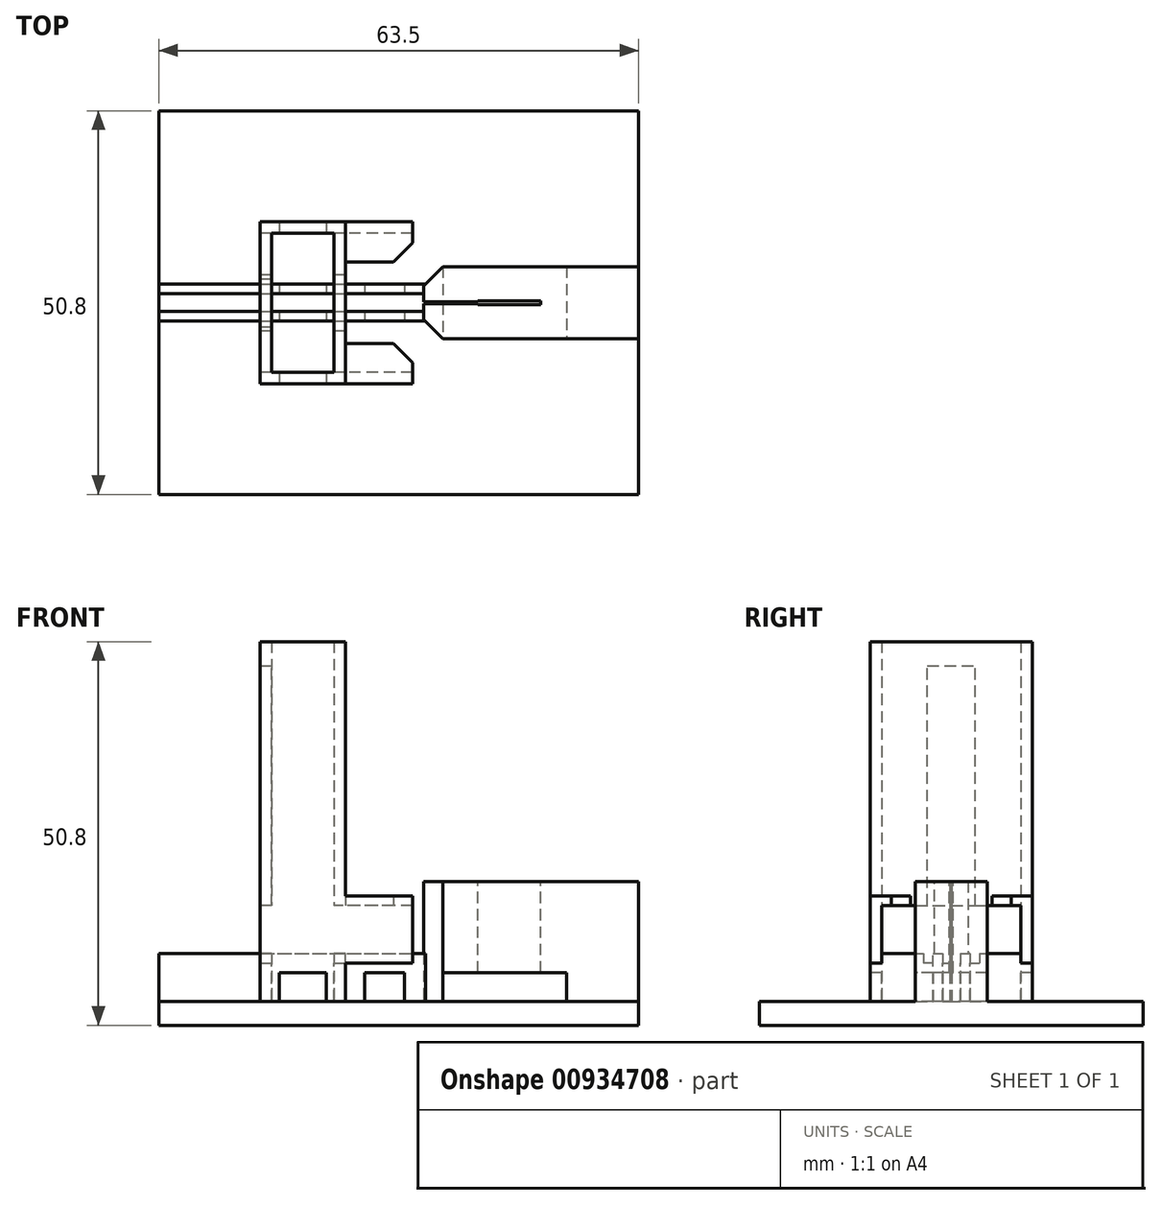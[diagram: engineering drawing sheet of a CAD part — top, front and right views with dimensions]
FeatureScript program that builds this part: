
annotation { "Feature Type Name" : "Feature", "Feature Type Description" : "" }
export const myFeature = defineFeature(function(context is Context, id is Id, definition is map)
    precondition{}
    {
        {
            var Q0;
            Q0=qCreatedBy(makeId("Top.planeOp"),FACE);
            var sketch = newSketch(context, id + "F0", { "sketchPlane" : qUnion([Q0])});
            skLineSegment(sketch, "E0.bottom", {"start": v(4.13, 9.2) * mm, "end": v(-4.13, 9.2) * mm});
            skLineSegment(sketch, "E0.top", {"start": v(4.13, -9.2) * mm, "end": v(-4.13, -9.2) * mm});
            skLineSegment(sketch, "E0.left", {"start": v(4.13, 9.2) * mm, "end": v(4.13, -9.2) * mm});
            skLineSegment(sketch, "E0.right", {"start": v(-4.13, 9.2) * mm, "end": v(-4.13, -9.2) * mm});
            skPoint(sketch, "E0.middle", {"position": v(0, 0) * mm});
            skLineSegment(sketch, "E1.bottom", {"start": v(5.65, 10.73) * mm, "end": v(-5.65, 10.73) * mm});
            skLineSegment(sketch, "E1.top", {"start": v(5.65, -10.73) * mm, "end": v(-5.65, -10.73) * mm});
            skLineSegment(sketch, "E1.left", {"start": v(5.65, 10.73) * mm, "end": v(5.65, -10.73) * mm});
            skLineSegment(sketch, "E1.right", {"start": v(-5.65, 10.73) * mm, "end": v(-5.65, -10.73) * mm});
            skSolve(sketch);
        }
        {
            var Q0;
            Q0 = qSketchRegion(id + "F0", true);
            extrude(context, id + "F1", {"entities" : qUnion([Q0]), "depth" : 50.8 * mm, "offsetDistance" : 25.4 * mm});
        }
        {
            var Q0;
            Q0=qCreatedBy(makeId("Right.planeOp"),FACE);
            var sketch = newSketch(context, id + "F2", { "sketchPlane" : qUnion([Q0])});
            skLineSegment(sketch, "E2.bottom", {"start": v(9.2, 15.88) * mm, "end": v(-9.2, 15.88) * mm});
            skLineSegment(sketch, "E2.top", {"start": v(9.2, 9.53) * mm, "end": v(-9.2, 9.53) * mm});
            skLineSegment(sketch, "E2.left", {"start": v(9.2, 15.88) * mm, "end": v(9.2, 9.53) * mm});
            skLineSegment(sketch, "E2.right", {"start": v(-9.2, 15.88) * mm, "end": v(-9.2, 9.53) * mm});
            skPoint(sketch, "E2.middle", {"position": v(0, 12.7) * mm});
            skSolve(sketch);
        }
        {
            var Q0;
            Q0 = qSketchRegion(id + "F2", true);
            extrude(context, id + "F3", {"entities" : qUnion([Q0]), "operationType" : NewBodyOperationType.REMOVE, "endBound" : BoundingType.SYMMETRIC, "depth" : 25.4 * mm, "offsetDistance" : 25.4 * mm});
        }
        {
            var Q0;
            Q0=qCreatedBy(makeId("Right.planeOp"),FACE);
            var sketch = newSketch(context, id + "F4", { "sketchPlane" : qUnion([Q0])});
            skLineSegment(sketch, "E3.bottom", {"start": v(-3.17, 15.88) * mm, "end": v(3.18, 15.88) * mm});
            skLineSegment(sketch, "E3.top", {"start": v(-3.18, 47.63) * mm, "end": v(3.17, 47.63) * mm});
            skLineSegment(sketch, "E3.left", {"start": v(-3.17, 15.88) * mm, "end": v(-3.18, 47.63) * mm});
            skLineSegment(sketch, "E3.right", {"start": v(3.18, 15.88) * mm, "end": v(3.17, 47.63) * mm});
            skLineSegment(sketch, "E4", {"start": v(0, 47.63) * mm, "end": v(0, 15.88) * mm, "construction": true});
            skSolve(sketch);
        }
        {
            var Q0;
            Q0 = qSketchRegion(id + "F4", true);
            extrude(context, id + "F5", {"entities" : qUnion([Q0]), "operationType" : NewBodyOperationType.REMOVE, "oppositeDirection" : true, "depth" : 25.4 * mm, "offsetDistance" : 25.4 * mm});
        }
        {
            var Q0;
            Q0=qCreatedBy(makeId("Top.planeOp"),FACE);
            var sketch = newSketch(context, id + "F6", { "sketchPlane" : qUnion([Q0])});
            skLineSegment(sketch, "E5.bottom", {"start": v(-19.05, -25.4) * mm, "end": v(44.45, -25.4) * mm});
            skLineSegment(sketch, "E5.top", {"start": v(-19.05, 25.4) * mm, "end": v(44.45, 25.4) * mm});
            skLineSegment(sketch, "E5.left", {"start": v(-19.05, -25.4) * mm, "end": v(-19.05, 25.4) * mm});
            skLineSegment(sketch, "E5.right", {"start": v(44.45, -25.4) * mm, "end": v(44.45, 25.4) * mm});
            skLineSegment(sketch, "E6", {"start": v(-19.05, 0) * mm, "end": v(44.45, 0) * mm, "construction": true});
            skSolve(sketch);
        }
        {
            var Q0;
            Q0 = qSketchRegion(id + "F6", true);
            extrude(context, id + "F7", {"entities" : qUnion([Q0]), "operationType" : NewBodyOperationType.ADD, "depth" : 3.17 * mm, "offsetDistance" : 25.4 * mm});
        }
        {
            var Q0;
            {var subQ0=sQuery(id+"F6.wireOp",EDGE,"E5.bottom");var subQ1=sQuery(id+"F6.wireOp",EDGE,"E5.top");var subQ2=sQuery(id+"F6.wireOp",EDGE,"E5.left");var subQ3=sQuery(id+"F6.wireOp",EDGE,"E5.right");Q0=makeQuery(id+"F7.boolean.opBoolean","SPLIT",FACE,{"disambiguationData":[TD([makeQuery(id+"F1.opExtrude","SWEPT_FACE",FACE,{"disambiguationData":[OSD([sQuery(id+"F0.wireOp",EDGE,"E1.bottom")])]})])],"derivedFrom":makeQuery(id+"F7.opExtrude","CAP_FACE",FACE,{"disambiguationData":[OSD([subQ0,subQ1,subQ2,subQ3])],"isStart":false})});}
            var sketch = newSketch(context, id + "F8", { "sketchPlane" : qUnion([Q0])});
            skLineSegment(sketch, "E7.bottom", {"start": v(16, -4.76) * mm, "end": v(44.45, -4.76) * mm});
            skLineSegment(sketch, "E7.top", {"start": v(16, 4.76) * mm, "end": v(44.45, 4.76) * mm});
            skLineSegment(sketch, "E7.left", {"start": v(16, -4.76) * mm, "end": v(16, 4.76) * mm});
            skLineSegment(sketch, "E7.right", {"start": v(44.45, -4.76) * mm, "end": v(44.45, 4.76) * mm});
            skLineSegment(sketch, "E8", {"start": v(16, 0) * mm, "end": v(44.45, 0) * mm, "construction": true});
            skSolve(sketch);
        }
        {
            var Q0;
            Q0 = qSketchRegion(id + "F8", true);
            extrude(context, id + "F9", {"entities" : qUnion([Q0]), "operationType" : NewBodyOperationType.ADD, "depth" : 15.88 * mm, "offsetDistance" : 25.4 * mm});
        }
        {
            var Q0;
            Q0=makeQuery(id+"F9.opExtrude","CAP_FACE",FACE,{"disambiguationData":[OSD([sQuery(id+"F8.wireOp",EDGE,"E7.bottom"),sQuery(id+"F8.wireOp",EDGE,"E7.top"),sQuery(id+"F8.wireOp",EDGE,"E7.left"),sQuery(id+"F8.wireOp",EDGE,"E7.right")])],"isStart":false});
            var sketch = newSketch(context, id + "F10", { "sketchPlane" : qUnion([Q0])});
            skLineSegment(sketch, "E9.left", {"start": v(11.68, -0.13) * mm, "end": v(11.68, 0.13) * mm});
            skLineSegment(sketch, "E9.right", {"start": v(31.5, -0.25) * mm, "end": v(31.5, 0.25) * mm});
            skLineSegment(sketch, "E10", {"start": v(11.68, 0) * mm, "end": v(31.5, 0) * mm, "construction": true});
            skLineSegment(sketch, "E11", {"start": v(11.68, 0.13) * mm, "end": v(23.16, 0.13) * mm});
            skLineSegment(sketch, "E12", {"start": v(23.16, 0.13) * mm, "end": v(23.16, 0.25) * mm});
            skLineSegment(sketch, "E13", {"start": v(23.16, 0.25) * mm, "end": v(31.5, 0.25) * mm});
            skLineSegment(sketch, "E14", {"start": v(11.68, -0.13) * mm, "end": v(23.16, -0.13) * mm});
            skLineSegment(sketch, "E15", {"start": v(23.16, -0.13) * mm, "end": v(23.16, -0.25) * mm});
            skLineSegment(sketch, "E16", {"start": v(23.16, -0.25) * mm, "end": v(31.5, -0.25) * mm});
            skSolve(sketch);
        }
        {
            var Q0;
            Q0 = qSketchRegion(id + "F10", true);
            var Q1;
            {var subQ0=sQuery(id+"F6.wireOp",EDGE,"E5.bottom");var subQ1=sQuery(id+"F6.wireOp",EDGE,"E5.top");var subQ2=sQuery(id+"F6.wireOp",EDGE,"E5.left");var subQ3=sQuery(id+"F6.wireOp",EDGE,"E5.right");Q1=makeQuery(id+"F7.boolean.opBoolean","SPLIT",FACE,{"disambiguationData":[TD([makeQuery(id+"F1.opExtrude","SWEPT_FACE",FACE,{"disambiguationData":[OSD([sQuery(id+"F0.wireOp",EDGE,"E1.bottom")])]})])],"derivedFrom":makeQuery(id+"F7.opExtrude","CAP_FACE",FACE,{"disambiguationData":[OSD([subQ0,subQ1,subQ2,subQ3])],"isStart":false})});}
            extrude(context, id + "F11", {"entities" : qUnion([Q0]), "operationType" : NewBodyOperationType.REMOVE, "endBound" : BoundingType.UP_TO_SURFACE, "oppositeDirection" : true, "depth" : 1.59 * mm, "endBoundEntityFace" : qUnion([Q1]), "offsetDistance" : 25.4 * mm});
        }
        {
            var Q0;
            {var subQ0=sQuery(id+"F6.wireOp",EDGE,"E5.bottom");var subQ1=sQuery(id+"F6.wireOp",EDGE,"E5.top");var subQ2=sQuery(id+"F6.wireOp",EDGE,"E5.left");var subQ3=sQuery(id+"F6.wireOp",EDGE,"E5.right");Q0=makeQuery(id+"F7.boolean.opBoolean","SPLIT",FACE,{"disambiguationData":[TD([makeQuery(id+"F1.opExtrude","SWEPT_FACE",FACE,{"disambiguationData":[OSD([sQuery(id+"F0.wireOp",EDGE,"E1.bottom")])]})])],"derivedFrom":makeQuery(id+"F7.opExtrude","CAP_FACE",FACE,{"disambiguationData":[OSD([subQ0,subQ1,subQ2,subQ3])],"isStart":false})});}
            var sketch = newSketch(context, id + "F12", { "sketchPlane" : qUnion([Q0])});
            skLineSegment(sketch, "E17.bottom", {"start": v(-19.05, 1.17) * mm, "end": v(16, 1.17) * mm});
            skLineSegment(sketch, "E17.top", {"start": v(-19.05, 2.44) * mm, "end": v(16, 2.44) * mm});
            skLineSegment(sketch, "E17.left", {"start": v(-19.05, 1.17) * mm, "end": v(-19.05, 2.44) * mm});
            skLineSegment(sketch, "E17.right", {"start": v(16, 1.17) * mm, "end": v(16, 2.44) * mm});
            skLineSegment(sketch, "E18.MirrorCS", {"start": v(-19.05, -1.17) * mm, "end": v(16, -1.17) * mm});
            skLineSegment(sketch, "E19.MirrorCS", {"start": v(-19.05, -2.44) * mm, "end": v(16, -2.44) * mm});
            skLineSegment(sketch, "E20.MirrorCS", {"start": v(-19.05, -1.17) * mm, "end": v(-19.05, -2.44) * mm});
            skLineSegment(sketch, "E21.MirrorCS", {"start": v(16, -1.17) * mm, "end": v(16, -2.44) * mm});
            skSolve(sketch);
        }
        {
            var Q0;
            Q0 = qSketchRegion(id + "F12", true);
            extrude(context, id + "F13", {"entities" : qUnion([Q0]), "operationType" : NewBodyOperationType.ADD, "depth" : 6.35 * mm, "offsetDistance" : 25.4 * mm});
        }
        {
            var Q0;
            {var subQ2=sQuery(id+"F0.wireOp",EDGE,"E1.left");var subQ3=makeQuery(id+"F1.opExtrude","SWEPT_FACE",FACE,{"disambiguationData":[OSD([subQ2])]});var subQ6=sQuery(id+"F0.wireOp",EDGE,"E0.bottom");var subQ7=makeQuery(id+"F1.opExtrude","SWEPT_FACE",FACE,{"disambiguationData":[OSD([subQ6])]});Q0=makeQuery(id+"F13.boolean.opBoolean","SPLIT",FACE,{"disambiguationData":[TD([subQ7])],"derivedFrom":subQ3});}
            var sketch = newSketch(context, id + "F14", { "sketchPlane" : qUnion([Q0])});
            skLineSegment(sketch, "E22.bottom", {"start": v(-2.44, 9.53) * mm, "end": v(-3.71, 9.53) * mm});
            skLineSegment(sketch, "E22.top", {"start": v(-2.44, 8.26) * mm, "end": v(-3.71, 8.26) * mm});
            skLineSegment(sketch, "E22.left", {"start": v(-2.44, 9.53) * mm, "end": v(-2.44, 8.26) * mm});
            skLineSegment(sketch, "E22.right", {"start": v(-3.71, 9.53) * mm, "end": v(-3.71, 8.26) * mm});
            skLineSegment(sketch, "E23.bottom", {"start": v(-1.17, 9.53) * mm, "end": v(1.17, 9.53) * mm});
            skLineSegment(sketch, "E23.top", {"start": v(-1.17, 8.26) * mm, "end": v(1.17, 8.26) * mm});
            skLineSegment(sketch, "E23.left", {"start": v(-1.17, 9.53) * mm, "end": v(-1.17, 8.26) * mm});
            skLineSegment(sketch, "E23.right", {"start": v(1.17, 9.53) * mm, "end": v(1.17, 8.26) * mm});
            skLineSegment(sketch, "E24.bottom", {"start": v(2.44, 9.53) * mm, "end": v(3.71, 9.53) * mm});
            skLineSegment(sketch, "E24.top", {"start": v(2.44, 8.26) * mm, "end": v(3.71, 8.26) * mm});
            skLineSegment(sketch, "E24.left", {"start": v(2.44, 9.53) * mm, "end": v(2.44, 8.26) * mm});
            skLineSegment(sketch, "E24.right", {"start": v(3.71, 9.53) * mm, "end": v(3.71, 8.26) * mm});
            skSolve(sketch);
        }
        {
            var Q0;
            Q0 = qSketchRegion(id + "F14", true);
            extrude(context, id + "F15", {"entities" : qUnion([Q0]), "operationType" : NewBodyOperationType.REMOVE, "endBound" : BoundingType.THROUGH_ALL, "oppositeDirection" : true, "depth" : 25.4 * mm, "offsetDistance" : 25.4 * mm});
        }
        {
            var Q0;
            Q0=makeQuery(id+"F1.opExtrude","SWEPT_FACE",FACE,{"disambiguationData":[OSD([sQuery(id+"F0.wireOp",EDGE,"E1.top")])]});
            var sketch = newSketch(context, id + "F16", { "sketchPlane" : qUnion([Q0])});
            skLineSegment(sketch, "E25.bottom", {"start": v(-3.11, 3.17) * mm, "end": v(3.11, 3.17) * mm});
            skLineSegment(sketch, "E25.top", {"start": v(-3.11, 6.98) * mm, "end": v(3.11, 6.98) * mm});
            skLineSegment(sketch, "E25.left", {"start": v(-3.11, 3.17) * mm, "end": v(-3.11, 6.98) * mm});
            skLineSegment(sketch, "E25.right", {"start": v(3.11, 3.17) * mm, "end": v(3.11, 6.98) * mm});
            skLineSegment(sketch, "E26.bottom", {"start": v(8.2, 3.17) * mm, "end": v(13.46, 3.17) * mm});
            skLineSegment(sketch, "E26.top", {"start": v(8.2, 6.99) * mm, "end": v(13.46, 6.99) * mm});
            skLineSegment(sketch, "E26.left", {"start": v(8.2, 3.17) * mm, "end": v(8.2, 6.99) * mm});
            skLineSegment(sketch, "E26.right", {"start": v(13.46, 3.17) * mm, "end": v(13.46, 6.99) * mm});
            skLineSegment(sketch, "E27.bottom", {"start": v(18.54, 3.17) * mm, "end": v(34.93, 3.18) * mm});
            skLineSegment(sketch, "E27.top", {"start": v(18.54, 6.99) * mm, "end": v(34.93, 6.99) * mm});
            skLineSegment(sketch, "E27.left", {"start": v(18.54, 3.17) * mm, "end": v(18.54, 6.99) * mm});
            skLineSegment(sketch, "E27.right", {"start": v(34.93, 3.18) * mm, "end": v(34.93, 6.99) * mm});
            skSolve(sketch);
        }
        {
            var Q0;
            Q0 = qSketchRegion(id + "F16", true);
            extrude(context, id + "F17", {"entities" : qUnion([Q0]), "operationType" : NewBodyOperationType.REMOVE, "endBound" : BoundingType.THROUGH_ALL, "oppositeDirection" : true, "depth" : 25.4 * mm, "offsetDistance" : 25.4 * mm});
        }
        {
            var Q0;
            {var subQ5=sQuery(id+"F0.wireOp",EDGE,"E0.bottom");var subQ6=makeQuery(id+"F1.opExtrude","SWEPT_FACE",FACE,{"disambiguationData":[OSD([subQ5])]});var subQ11=sQuery(id+"F0.wireOp",EDGE,"E1.left");var subQ12=makeQuery(id+"F1.opExtrude","SWEPT_FACE",FACE,{"disambiguationData":[OSD([subQ11])]});Q0=makeQuery(id+"F13.boolean.opBoolean","SPLIT",FACE,{"disambiguationData":[TD([subQ6])],"derivedFrom":subQ12});}
            var sketch = newSketch(context, id + "F18", { "sketchPlane" : qUnion([Q0])});
            skLineSegment(sketch, "E28", {"start": v(-5.4, 15.88) * mm, "end": v(-9.2, 15.88) * mm});
            skLineSegment(sketch, "E29", {"start": v(-9.2, 15.88) * mm, "end": v(-9.2, 8.26) * mm});
            skLineSegment(sketch, "E30", {"start": v(-9.2, 8.26) * mm, "end": v(-10.73, 8.26) * mm});
            skLineSegment(sketch, "E31", {"start": v(-10.73, 8.26) * mm, "end": v(-10.73, 17.15) * mm});
            skLineSegment(sketch, "E32", {"start": v(-10.73, 17.15) * mm, "end": v(-5.4, 17.15) * mm});
            skLineSegment(sketch, "E33", {"start": v(-5.4, 17.15) * mm, "end": v(-5.4, 15.88) * mm});
            skLineSegment(sketch, "E34.MirrorCS", {"start": v(5.4, 17.15) * mm, "end": v(5.4, 15.88) * mm});
            skLineSegment(sketch, "E35.MirrorCS", {"start": v(5.4, 15.88) * mm, "end": v(9.2, 15.88) * mm});
            skLineSegment(sketch, "E36.MirrorCS", {"start": v(9.2, 15.88) * mm, "end": v(9.2, 8.26) * mm});
            skLineSegment(sketch, "E37.MirrorCS", {"start": v(9.2, 8.26) * mm, "end": v(10.73, 8.26) * mm});
            skLineSegment(sketch, "E38.MirrorCS", {"start": v(10.73, 8.26) * mm, "end": v(10.73, 17.15) * mm});
            skLineSegment(sketch, "E39.MirrorCS", {"start": v(10.73, 17.15) * mm, "end": v(5.4, 17.15) * mm});
            skSolve(sketch);
        }
        {
            var Q0;
            Q0 = qSketchRegion(id + "F18", true);
            extrude(context, id + "F19", {"entities" : qUnion([Q0]), "operationType" : NewBodyOperationType.ADD, "depth" : 8.9 * mm, "offsetDistance" : 25.4 * mm});
        }
        {
            var Q0;
            Q0=makeQuery(id+"F9.opExtrude","SWEPT_EDGE",EDGE,{"disambiguationData":[OSD([sQuery(id+"F8.wireOp",EDGE,"E7.bottom"),sQuery(id+"F8.wireOp",EDGE,"E7.left")])]});
            var Q1;
            Q1=makeQuery(id+"F9.opExtrude","SWEPT_EDGE",EDGE,{"disambiguationData":[OSD([sQuery(id+"F8.wireOp",EDGE,"E7.top"),sQuery(id+"F8.wireOp",EDGE,"E7.left")])]});
            var Q2;
            Q2=makeQuery(id+"F19.opExtrude","CAP_EDGE",EDGE,{"disambiguationData":[OSD([sQuery(id+"F18.wireOp",EDGE,"E34.MirrorCS")])],"isStart":false});
            var Q3;
            Q3=makeQuery(id+"F19.opExtrude","CAP_EDGE",EDGE,{"disambiguationData":[OSD([sQuery(id+"F18.wireOp",EDGE,"E33")])],"isStart":false});
            chamfer(context, id + "F20", {"entities" : qUnion([Q0, Q1, Q2, Q3]), "width" : 2.54 * mm, "tangentPropagation" : true});
        }
    });
